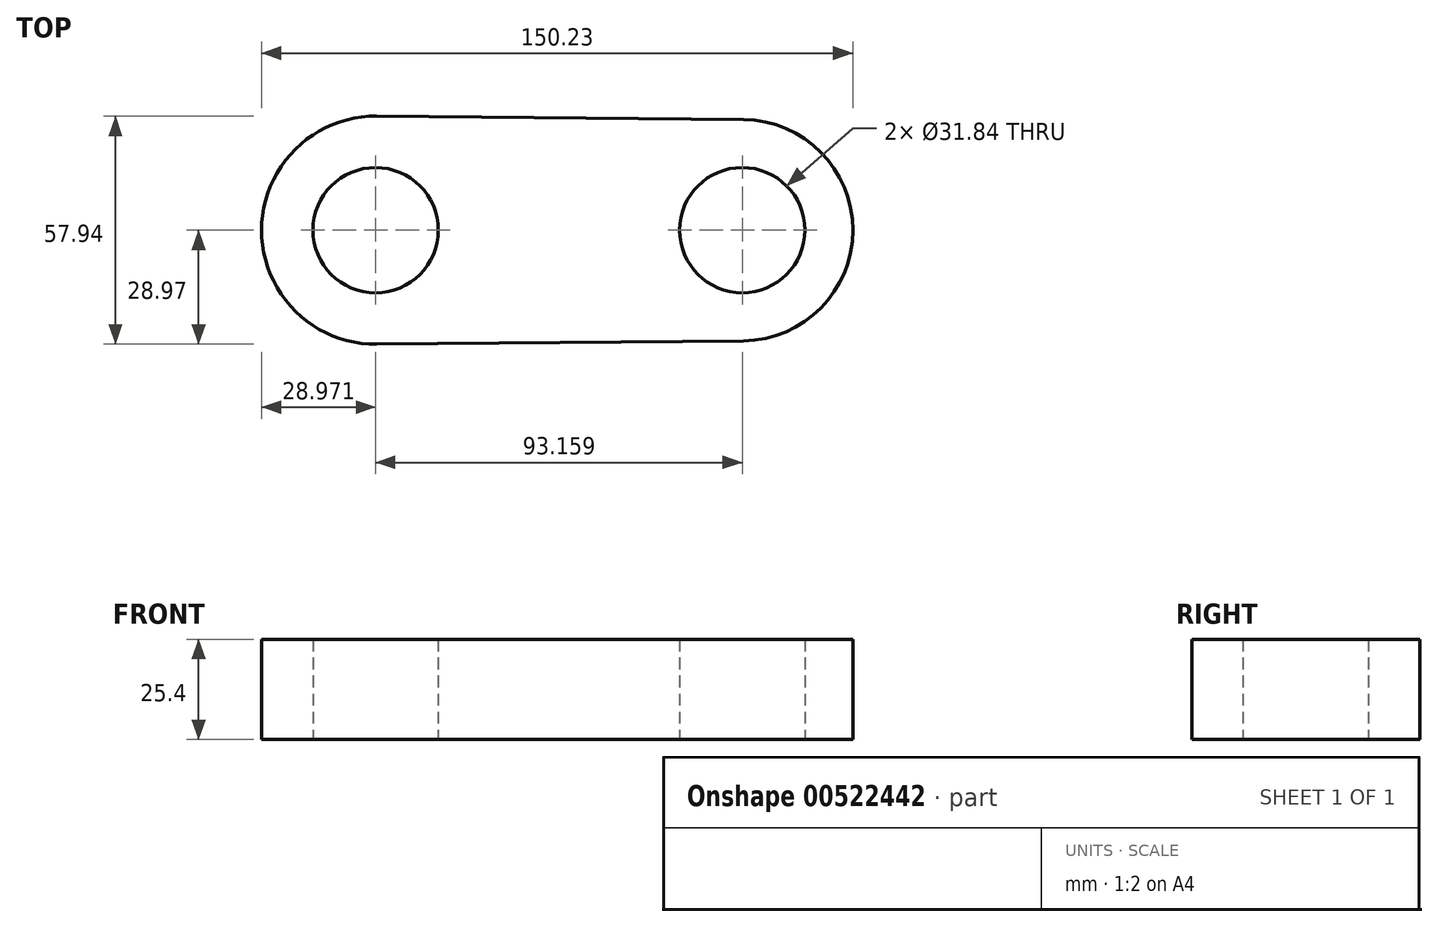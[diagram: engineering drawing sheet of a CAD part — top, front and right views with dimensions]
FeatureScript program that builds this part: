
annotation { "Feature Type Name" : "Feature", "Feature Type Description" : "" }
export const myFeature = defineFeature(function(context is Context, id is Id, definition is map)
    precondition{}
    {
        {
            var Q0;
            Q0=qCreatedBy(makeId("Top.planeOp"),FACE);
            var sketch = newSketch(context, id + "F0", { "sketchPlane" : qUnion([Q0])});
            skCircle(sketch, "E0", {"center": v(-46.58, 0) * mm, "radius": 15.92 * mm});
            skCircle(sketch, "E1", {"center": v(46.58, 0) * mm, "radius": 15.92 * mm});
            skArc(sketch, "E2", {"start": v(-46.3, 28.97) * mm, "mid": v(-75.55, 0) * mm, "end": v(-46.3, -28.97) * mm});
            skArc(sketch, "E3", {"start": v(46.84, -28.1) * mm, "mid": v(74.68, 0) * mm, "end": v(46.84, 28.1) * mm});
            skLineSegment(sketch, "E4", {"start": v(-46.3, 28.97) * mm, "end": v(46.84, 28.1) * mm});
            skLineSegment(sketch, "E5", {"start": v(46.84, -28.1) * mm, "end": v(-46.3, -28.97) * mm});
            skArc(sketch, "E6", {"start": v(-46.3, -28.97) * mm, "mid": v(-17.6, 0) * mm, "end": v(-46.3, 28.97) * mm});
            skSolve(sketch);
        }
        {
            var Q0;
            Q0=makeQuery(id+"F0.imprint","IMPRINT",FACE,{"disambiguationData":[TD([[makeQuery(id+"F0.imprint","IMPRINT",EDGE,{"derivedFrom":sQuery(id+"F0.wireOp",EDGE,"E0")}),-1.0]])]});
            var Q1;
            Q1=makeQuery(id+"F0.imprint","IMPRINT",FACE,{"disambiguationData":[TD([[makeQuery(id+"F0.imprint","IMPRINT",EDGE,{"derivedFrom":sQuery(id+"F0.wireOp",EDGE,"E1")}),-1.0]])]});
            extrude(context, id + "F1", {"entities" : qUnion([Q0, Q1]), "depth" : 25.4 * mm, "offsetDistance" : 25.4 * mm});
        }
    });
